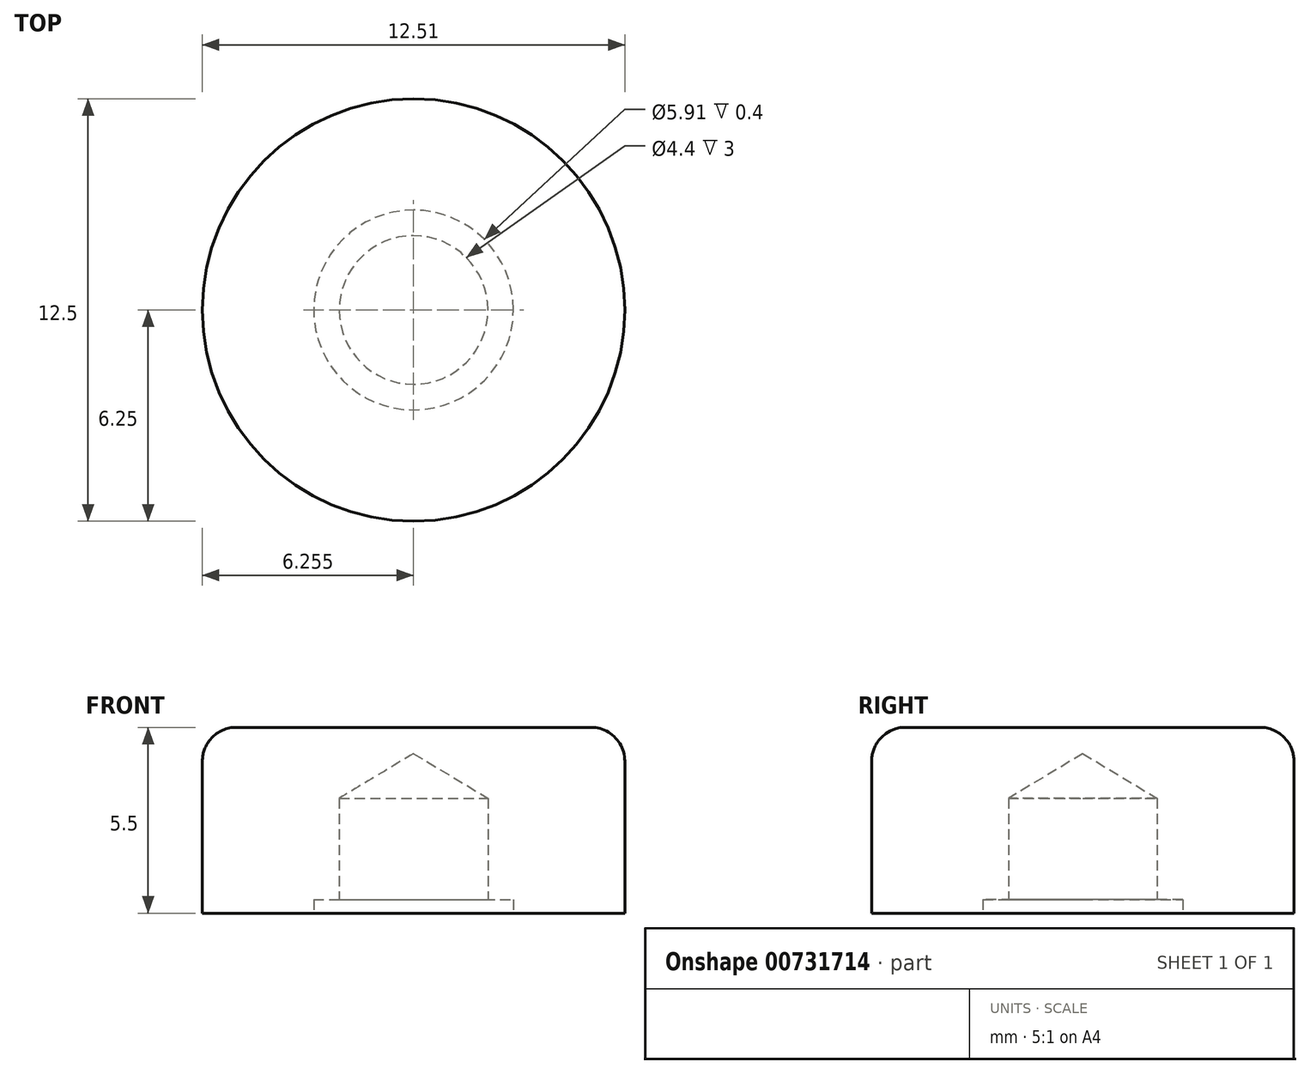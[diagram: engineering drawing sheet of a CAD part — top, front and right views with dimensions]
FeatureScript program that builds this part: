
annotation { "Feature Type Name" : "Feature", "Feature Type Description" : "" }
export const myFeature = defineFeature(function(context is Context, id is Id, definition is map)
    precondition{}
    {
        {
            var Q0;
            Q0=qCreatedBy(makeId("Front.planeOp"),FACE);
            var sketch = newSketch(context, id + "F0", { "sketchPlane" : qUnion([Q0])});
            skLineSegment(sketch, "E0", {"start": v(0, 0) * mm, "end": v(0, 6.26) * mm});
            skLineSegment(sketch, "E1", {"start": v(-6.35, 0) * mm, "end": v(-6.35, 2.38) * mm});
            skLineSegment(sketch, "E2", {"start": v(-6.35, 2.38) * mm, "end": v(-5.23, 2.38) * mm});
            skLineSegment(sketch, "E3", {"start": v(-5.23, 2.38) * mm, "end": v(-5.23, 3.88) * mm});
            skLineSegment(sketch, "E4", {"start": v(-6.35, 0) * mm, "end": v(-8.35, 0) * mm});
            skLineSegment(sketch, "E5", {"start": v(-5.23, 3.88) * mm, "end": v(-8.35, 3.88) * mm});
            skLineSegment(sketch, "E6", {"start": v(-8.35, 3.88) * mm, "end": v(-8.35, 1.8) * mm});
            skLineSegment(sketch, "E7", {"start": v(-8.35, 1.8) * mm, "end": v(-28.58, 1.8) * mm});
            skLineSegment(sketch, "E8", {"start": v(-28.58, 1.8) * mm, "end": v(-28.58, 0) * mm});
            skLineSegment(sketch, "E9", {"start": v(-28.58, 0) * mm, "end": v(-8.35, 0) * mm});
            skLineSegment(sketch, "E10", {"start": v(-3.18, 0) * mm, "end": v(-3.18, -2.38) * mm});
            skLineSegment(sketch, "E11", {"start": v(0, 10.42) * mm, "end": v(-12, 10.42) * mm});
            skLineSegment(sketch, "E12", {"start": v(-4.17, 4.88) * mm, "end": v(-12, 4.88) * mm});
            skPoint(sketch, "E13.end.orphan", {"position": v(-28.58, 6.26) * mm});
            skPoint(sketch, "E14.end.orphan", {"position": v(-3.18, 3.88) * mm});
            skLineSegment(sketch, "E15", {"start": v(-3.18, 0) * mm, "end": v(-3.18, 2.38) * mm});
            skLineSegment(sketch, "E16", {"start": v(-3.18, 2.38) * mm, "end": v(-4.17, 2.38) * mm});
            skLineSegment(sketch, "E17", {"start": v(-4.17, 2.38) * mm, "end": v(-4.17, 4.88) * mm});
            skLineSegment(sketch, "E18", {"start": v(-12, 4.88) * mm, "end": v(-12, 8.38) * mm});
            skLineSegment(sketch, "E19", {"start": v(-12, 8.38) * mm, "end": v(-8.91, 8.38) * mm});
            skLineSegment(sketch, "E20", {"start": v(0, 7.1) * mm, "end": v(0, -2.38) * mm});
            skLineSegment(sketch, "E21", {"start": v(0, -2.38) * mm, "end": v(-3.18, -2.38) * mm});
            skArc(sketch, "E22", {"start": v(-8.91, 8.38) * mm, "mid": v(-4.5, 7.4) * mm, "end": v(0, 7.1) * mm});
            skPoint(sketch, "E23.orphan", {"position": v(0, 8.38) * mm});
            skSolve(sketch);
        }
        {
            var Q0;
            Q0=makeQuery(id+"F0.imprint","IMPRINT",FACE,{"disambiguationData":[TD([[makeQuery(id+"F0.imprint","IMPRINT",EDGE,{"derivedFrom":sQuery(id+"F0.wireOp",EDGE,"E1")}),1.0]])]});
            var Q1;
            Q1=makeQuery(id+"F0.imprint","IMPRINT",FACE,{"disambiguationData":[TD([[makeQuery(id+"F0.imprint","IMPRINT",EDGE,{"derivedFrom":sQuery(id+"F0.wireOp",EDGE,"E10")}),1.0]])]});
            var Q2;
            Q2=sQuery(id+"F0.wireOp",EDGE,"E0");
            revolve(context, id + "F1", {"surfaceOperationType" : NewSurfaceOperationType.NEW, "entities" : qUnion([Q0, Q1]), "axis" : qUnion([Q2]), "revolveType" : RevolveType.FULL});
        }
        {
            var Q0;
            Q0=makeQuery(id+"F1.opRevolve","SWEPT_FACE",FACE,{"disambiguationData":[OSD([sQuery(id+"F0.wireOp",EDGE,"E7")])]});
            var sketch = newSketch(context, id + "F2", { "sketchPlane" : qUnion([Q0])});
            skCircle(sketch, "E24", {"center": v(-22.33, 0) * mm, "radius": 6.25 * mm});
            skArc(sketch, "E25", {"start": v(0, 12) * mm, "mid": v(-12.91, 11.4) * mm, "end": v(-24.57, 5.83) * mm});
            skArc(sketch, "E26.MirrorCS", {"start": v(0, -12) * mm, "mid": v(-12.91, -11.4) * mm, "end": v(-24.57, -5.83) * mm});
            skCircle(sketch, "E27.0", {"center": v(0, 0) * mm, "radius": 11.35 * mm});
            skArc(sketch, "E28.0", {"start": v(-0.46, -9.04) * mm, "mid": v(-12.18, -8.5) * mm, "end": v(-22.77, -3.43) * mm});
            skArc(sketch, "E29.0", {"start": v(-0.46, 9.04) * mm, "mid": v(-12.18, 8.5) * mm, "end": v(-22.77, 3.43) * mm});
            skPoint(sketch, "E30.start.orphan", {"position": v(-12, 0) * mm});
            skLineSegment(sketch, "E31", {"start": v(0, 2.89) * mm, "end": v(0, -2.96) * mm});
            skArc(sketch, "E32.MirrorCS", {"start": v(0.46, -9.04) * mm, "mid": v(12.18, -8.5) * mm, "end": v(22.77, -3.43) * mm});
            skArc(sketch, "E33.MirrorCS", {"start": v(0, -12) * mm, "mid": v(12.91, -11.4) * mm, "end": v(24.57, -5.83) * mm});
            skArc(sketch, "E34.MirrorCS", {"start": v(0.46, 9.04) * mm, "mid": v(12.18, 8.5) * mm, "end": v(22.77, 3.43) * mm});
            skArc(sketch, "E35.MirrorCS", {"start": v(0, 12) * mm, "mid": v(12.91, 11.4) * mm, "end": v(24.57, 5.83) * mm});
            skCircle(sketch, "E36.MirrorC", {"center": v(22.33, 0) * mm, "radius": 6.25 * mm});
            skCircle(sketch, "E37", {"center": v(22.33, 0) * mm, "radius": 2.96 * mm});
            skCircle(sketch, "E38.MirrorC", {"center": v(-22.33, 0) * mm, "radius": 2.96 * mm});
            skSolve(sketch);
        }
        {
            var Q0;
            {var subQ4=sQuery(id+"F2.wireOp",EDGE,"E26.MirrorCS");Q0=makeQuery(id+"F2.imprint","IMPRINT",FACE,{"disambiguationData":[TD([[makeQuery(id+"F2.imprint","IMPRINT",EDGE,{"derivedFrom":subQ4}),1.0]])]});}
            var Q1;
            Q1=makeQuery(id+"F2.imprint","IMPRINT",FACE,{"disambiguationData":[TD([[makeQuery(id+"F2.imprint","IMPRINT",EDGE,{"derivedFrom":sQuery(id+"F2.wireOp",EDGE,"E37")}),1.0]])]});
            var Q2;
            {var subQ0=sQuery(id+"F2.wireOp",EDGE,"E34.MirrorCS");var subQ1=sQuery(id+"F2.wireOp",EDGE,"E27.0");var subQ2=makeQuery(id+"F2.imprint","INTERSECT",VERTEX,{"derivedFrom":[subQ1,subQ0]});Q2=makeQuery(id+"F2.imprint","IMPRINT",FACE,{"disambiguationData":[TD([[makeQuery(id+"F2.imprint","IMPRINT",EDGE,{"disambiguationData":[TD([[subQ2,1.0]])],"derivedFrom":subQ1}),-1.0]])]});}
            var Q3;
            {var subQ0=sQuery(id+"F2.wireOp",EDGE,"E29.0");var subQ1=sQuery(id+"F2.wireOp",EDGE,"E24");var subQ2=makeQuery(id+"F2.imprint","INTERSECT",VERTEX,{"derivedFrom":[subQ1,subQ0]});Q3=makeQuery(id+"F2.imprint","IMPRINT",FACE,{"disambiguationData":[TD([[makeQuery(id+"F2.imprint","IMPRINT",EDGE,{"disambiguationData":[TD([[subQ2,1.0]])],"derivedFrom":subQ1}),-1.0]])]});}
            var Q4;
            Q4=makeQuery(id+"F2.imprint","IMPRINT",FACE,{"disambiguationData":[TD([[makeQuery(id+"F2.imprint","IMPRINT",EDGE,{"derivedFrom":sQuery(id+"F2.wireOp",EDGE,"E38.MirrorC")}),-1.0]])]});
            var Q5;
            {var subQ4=sQuery(id+"F2.wireOp",EDGE,"E25");Q5=makeQuery(id+"F2.imprint","IMPRINT",FACE,{"disambiguationData":[TD([[makeQuery(id+"F2.imprint","IMPRINT",EDGE,{"derivedFrom":subQ4}),-1.0]])]});}
            extrude(context, id + "F3", {"entities" : qUnion([Q0, Q1, Q2, Q3, Q4, Q5]), "operationType" : NewBodyOperationType.REMOVE, "oppositeDirection" : true, "depth" : 25 * mm, "offsetDistance" : 25 * mm});
        }
        {
            var Q0;
            Q0=makeQuery(id+"F1.opRevolve","SWEPT_EDGE",EDGE,{"disambiguationData":[OSD([sQuery(id+"F0.wireOp",EDGE,"E5"),sQuery(id+"F0.wireOp",EDGE,"E6")])]});
            fillet(context, id + "F4", {"entities" : qUnion([Q0]), "radius" : 1 * mm, "tangentPropagation" : true, "allowEdgeOverflow" : false});
        }
        {
            var Q0;
            Q0=makeQuery(id+"F1.opRevolve","SWEPT_EDGE",EDGE,{"disambiguationData":[OSD([sQuery(id+"F0.wireOp",EDGE,"E18"),sQuery(id+"F0.wireOp",EDGE,"E19")])]});
            fillet(context, id + "F5", {"entities" : qUnion([Q0]), "radius" : 1 * mm, "tangentPropagation" : true, "allowEdgeOverflow" : false});
        }
        {
            var Q0;
            Q0=makeQuery(id+"F2.imprint","IMPRINT",FACE,{"disambiguationData":[TD([[makeQuery(id+"F2.imprint","IMPRINT",EDGE,{"derivedFrom":sQuery(id+"F2.wireOp",EDGE,"E38.MirrorC")}),1.0]])]});
            var Q1;
            Q1=makeQuery(id+"F2.imprint","IMPRINT",FACE,{"disambiguationData":[TD([[makeQuery(id+"F2.imprint","IMPRINT",EDGE,{"derivedFrom":sQuery(id+"F2.wireOp",EDGE,"E38.MirrorC")}),-1.0]])]});
            extrude(context, id + "F6", {"entities" : qUnion([Q0, Q1]), "depth" : 5.5 * mm, "offsetDistance" : 25 * mm});
        }
        {
            var Q0;
            Q0=makeQuery(id+"F6.opExtrude","CAP_EDGE",EDGE,{"disambiguationData":[OSD([sQuery(id+"F2.wireOp",EDGE,"E24")])],"isStart":false});
            fillet(context, id + "F7", {"entities" : qUnion([Q0]), "radius" : 1 * mm, "tangentPropagation" : true, "allowEdgeOverflow" : false});
        }
        {
            var Q0;
            Q0=makeQuery(id+"F6.opExtrude","CAP_FACE",FACE,{"disambiguationData":[OSD([sQuery(id+"F2.wireOp",EDGE,"E24")])],"isStart":true});
            var sketch = newSketch(context, id + "F8", { "sketchPlane" : qUnion([Q0])});
            skCircle(sketch, "E39", {"center": v(-22.33, 0) * mm, "radius": 2.96 * mm});
            skSolve(sketch);
        }
        {
            var Q0;
            Q0=qSketchRegion(id+"F8",true);
            extrude(context, id + "F9", {"entities" : qUnion([Q0]), "operationType" : NewBodyOperationType.REMOVE, "oppositeDirection" : true, "depth" : .4 * mm, "offsetDistance" : 25 * mm});
        }
        {
            var Q0;
            Q0=makeQuery(id+"F1.opRevolve","SWEPT_BODY",BODY,{"disambiguationData":[OSD([sQuery(id+"F0.wireOp",EDGE,"E1"),sQuery(id+"F0.wireOp",EDGE,"E2"),sQuery(id+"F0.wireOp",EDGE,"E3"),sQuery(id+"F0.wireOp",EDGE,"E4"),sQuery(id+"F0.wireOp",EDGE,"E5"),sQuery(id+"F0.wireOp",EDGE,"E6"),sQuery(id+"F0.wireOp",EDGE,"E7"),sQuery(id+"F0.wireOp",EDGE,"E8"),sQuery(id+"F0.wireOp",EDGE,"E9")])]});
            deleteBodies(context, id + "F10", {"entities" : qUnion([Q0])});
        }
        {
            var Q0;
            Q0=makeQuery(id+"F1.opRevolve","SWEPT_BODY",BODY,{"disambiguationData":[OSD([sQuery(id+"F0.wireOp",EDGE,"E10"),sQuery(id+"F0.wireOp",EDGE,"E12"),sQuery(id+"F0.wireOp",EDGE,"E15"),sQuery(id+"F0.wireOp",EDGE,"E16"),sQuery(id+"F0.wireOp",EDGE,"E17"),sQuery(id+"F0.wireOp",EDGE,"E18"),sQuery(id+"F0.wireOp",EDGE,"E19"),sQuery(id+"F0.wireOp",EDGE,"E20"),sQuery(id+"F0.wireOp",EDGE,"E21"),sQuery(id+"F0.wireOp",EDGE,"E22")])]});
            deleteBodies(context, id + "F11", {"entities" : qUnion([Q0])});
        }
        {
            var Q0;
            Q0=makeQuery(id+"F9.boolean.opBoolean","COPY",FACE,{"derivedFrom":makeQuery(id+"F9.opExtrude","CAP_FACE",FACE,{"disambiguationData":[OSD([sQuery(id+"F8.wireOp",EDGE,"E39")])],"isStart":false})});
            var sketch = newSketch(context, id + "F12", { "sketchPlane" : qUnion([Q0])});
            skPoint(sketch, "E40", {"position": v(-22.33, 0) * mm});
            skSolve(sketch);
        }
        {
            var Q0;
            Q0=sQuery(id+"F12.wireOp",VERTEX,"E40");
            var Q1;
            Q1=makeQuery(id+"F6.opExtrude","SWEPT_BODY",BODY,{"disambiguationData":[OSD([sQuery(id+"F2.wireOp",EDGE,"E24")])]});
            hole(context, id + "F13", {"style" : HoleStyle.SIMPLE, "endStyle" : HoleEndStyle.BLIND, "standardTappedOrClearance" : lookupTablePath({ "standard" : "ISO", "fit" : "Normal", "size" : "M4", "type" : "Clearance" }), "standardBlindInLast" : lookupTablePath({ "fit" : "Standard", "standard" : "ISO", "size" : "M4", "type" : "Clearance" }), "holeDiameter" : 4.4 * mm, "majorDiameter" : 5 * mm, "holeDepth" : 3 * mm, "isTappedThrough" : true, "tappedDepth" : 12 * mm, "tapClearance" : 3, "locations" : qUnion([Q0]), "scope" : qUnion([Q1])});
        }
    });
